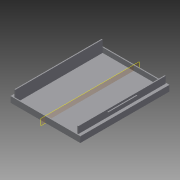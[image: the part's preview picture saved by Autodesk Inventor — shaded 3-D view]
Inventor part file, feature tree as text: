
AUTODESK INVENTOR PART (.ipt)
format: ipt  version: 2015 SP2 (Build 190223200, 223)  size: 141,824 bytes
history: native  units: in
note: dims shown in document units (in); Inventor stores cm internally (conversion verified against a paired STEP export)
features: extrude x6, sketch x5, projected_geometry x4, plane x1, mirror x1
ambient origin geometry x8: Origin, YZ Plane, XZ Plane, XY Plane, X Axis, Y Axis, Z Axis, Center Point
bodies: Solid1 (feature_tree)
feature tree (17):
  extrude  "Extrusion1"  Depth=3.622in
  extrude  "Extrusion2"  Depth=0.0394in
  extrude  "Extrusion3"  Depth=0.0197in
  plane  "Work Plane1"
  extrude  "Extrusion5"  Depth=0.0394in
  mirror  "Mirror2"
  extrude  "Extrusion6"  Depth=0.4724in TaperAngle=0.0deg
  extrude  "Extrusion7"  [1 undecoded]
  sketch  "Sketch1"  dims[d0=2.7165in d1=3.622in]
  sketch  "Sketch2"  dims[d2=0.0394in d3=0.0in d4=0.0394in]
  projected_geometry  "Projected Loop1"
  sketch  "Sketch3"  dims[d5=0.0197in d6=0.0197in]
  projected_geometry  "Projected Loop2"
  sketch  "Sketch5"  dims[d7=0.1969in d8=0.0in d9=0.0394in]
  projected_geometry  "Projected Loop3"
  sketch  "Sketch6"  dims[d10=0.0394in d11=0.4724in d12=0.0in d18=-1.3583in d21=0.0394in d22=0.0787in d23=0.1575in d24=1.1811in d25=1.1811in d26=0.0394in d27=0.0in d28=0.0591in d29=0.0in d30=0.0591in d31=0.0in]
  projected_geometry  "Projected Loop4"
note: 1 required parameter value undecoded (feature->parameter linkage not recoverable at this tier; creation-order binding heuristic only, values carry confidence <= 0.55)
